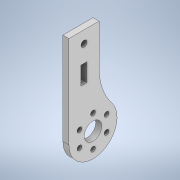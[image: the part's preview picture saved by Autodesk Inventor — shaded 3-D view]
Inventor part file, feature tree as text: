
AUTODESK INVENTOR PART (.ipt)
format: ipt  version: 2022 (Build 260153000, 153)  size: 150,528 bytes
history: native  units: mm
features: extrude x1, sketch x1
ambient origin geometry x8: Origin, YZ Plane, XZ Plane, XY Plane, X Axis, Y Axis, Z Axis, Center Point
bodies: Solid1 (feature_tree)
feature tree (2):
  extrude  "Extrusion1"  Depth=12.0mm
  sketch  "Sketch1"  dims[d1=60.0mm d2=24.0mm d3=8.75mm d4=18.0mm d5=1.2mm d7=360.0deg d8=45.0mm d12=12.0mm d15=58.0mm d16=15.0mm d18=30.0mm d19=3.0mm d20=0.0mm d22=3.0mm d23=6.0mm d28=7.5mm d29=15.0mm d31=9.0mm d32=3.0mm d33=12.0mm d30=0.5mm]
